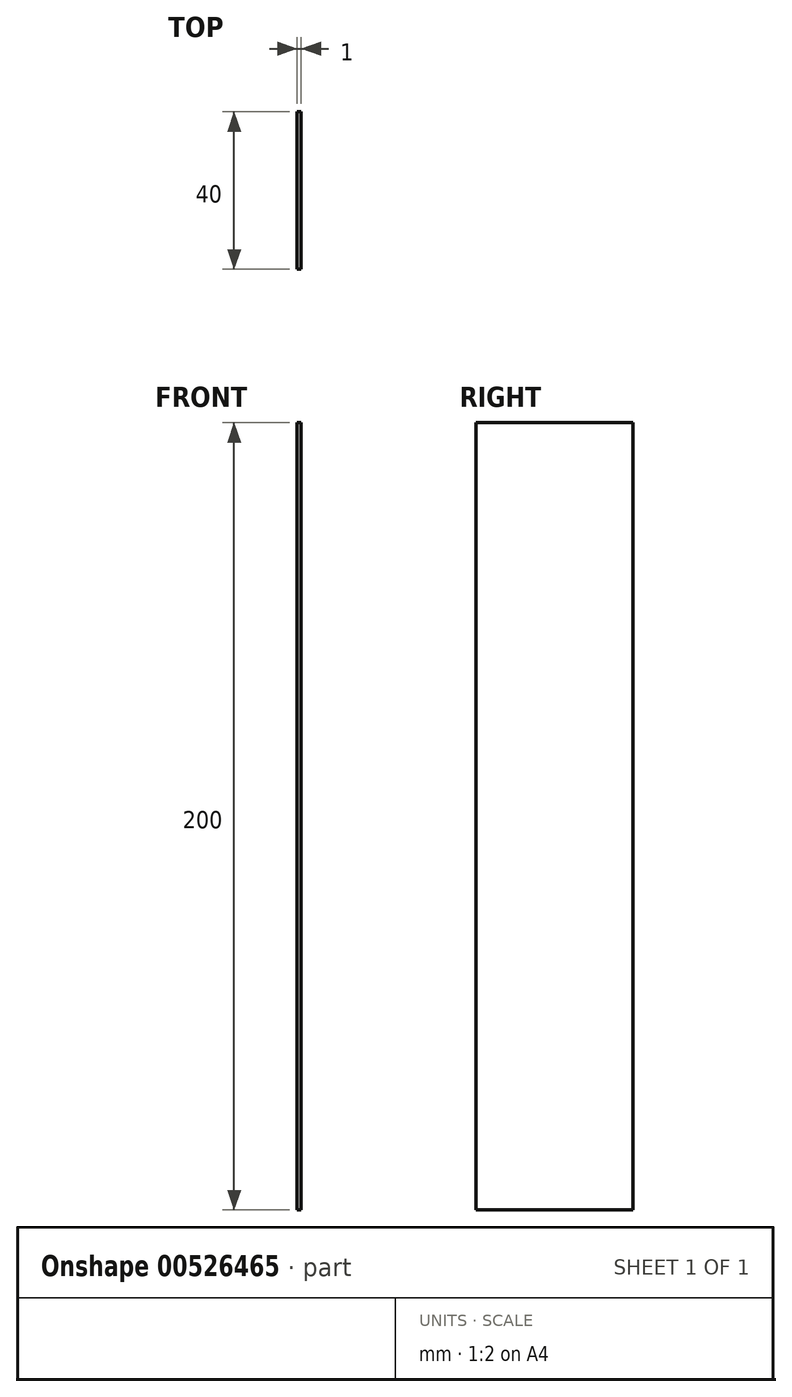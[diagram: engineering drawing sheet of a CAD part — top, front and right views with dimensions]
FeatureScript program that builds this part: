
annotation { "Feature Type Name" : "Feature", "Feature Type Description" : "" }
export const myFeature = defineFeature(function(context is Context, id is Id, definition is map)
    precondition{}
    {
        {
            var Q0;
            Q0=qCreatedBy(makeId("Right.planeOp"),FACE);
            var sketch = newSketch(context, id + "F0", { "sketchPlane" : qUnion([Q0])});
            skLineSegment(sketch, "E0.bottom", {"start": v(-20, 100) * mm, "end": v(20, 100) * mm});
            skLineSegment(sketch, "E0.top", {"start": v(-20, -100) * mm, "end": v(20, -100) * mm});
            skLineSegment(sketch, "E0.left", {"start": v(-20, 100) * mm, "end": v(-20, -100) * mm});
            skLineSegment(sketch, "E0.right", {"start": v(20, 100) * mm, "end": v(20, -100) * mm});
            skPoint(sketch, "E0.middle", {"position": v(0, 0) * mm});
            skSolve(sketch);
        }
        {
            var Q0;
            Q0 = qSketchRegion(id + "F0", true);
            extrude(context, id + "F1", {"entities" : qUnion([Q0]), "depth" : 1 * mm, "offsetDistance" : 25 * mm});
        }
    });
